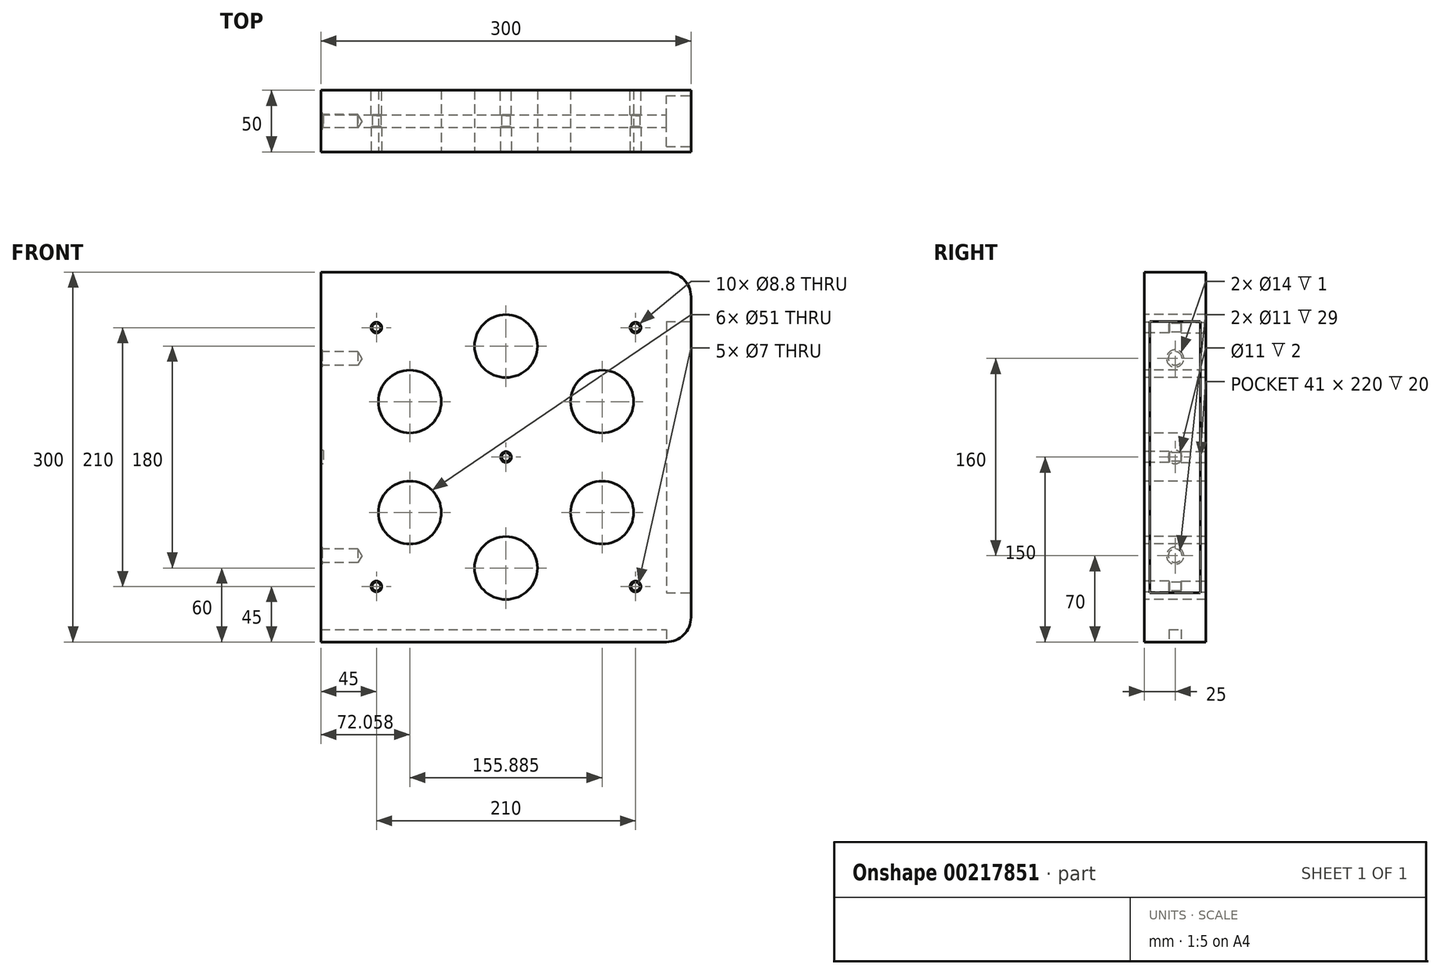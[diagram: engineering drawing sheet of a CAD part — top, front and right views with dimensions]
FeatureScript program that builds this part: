
annotation { "Feature Type Name" : "Feature", "Feature Type Description" : "" }
export const myFeature = defineFeature(function(context is Context, id is Id, definition is map)
    precondition{}
    {
        {
            var Q0;
            Q0=qCreatedBy(makeId("Front.planeOp"),FACE);
            var sketch = newSketch(context, id + "F0", { "sketchPlane" : qUnion([Q0])});
            skLineSegment(sketch, "E0.bottom", {"start": v(-150, 150) * mm, "end": v(150, 150) * mm});
            skLineSegment(sketch, "E0.top", {"start": v(-150, -150) * mm, "end": v(150, -150) * mm});
            skLineSegment(sketch, "E0.left", {"start": v(-150, 150) * mm, "end": v(-150, -150) * mm});
            skLineSegment(sketch, "E0.right", {"start": v(150, 150) * mm, "end": v(150, -150) * mm});
            skPoint(sketch, "E0.middle", {"position": v(0, 0) * mm});
            skSolve(sketch);
        }
        {
            var Q0;
            Q0=qSketchRegion(id+"F0",true);
            extrude(context, id + "F1", {"entities" : qUnion([Q0]), "depth" : 50 * mm});
        }
        {
            var Q0;
            Q0=makeQuery(id+"F1.opExtrude","CAP_FACE",FACE,{"disambiguationData":[OSD([sQuery(id+"F0.wireOp",EDGE,"E0.bottom"),sQuery(id+"F0.wireOp",EDGE,"E0.top"),sQuery(id+"F0.wireOp",EDGE,"E0.left"),sQuery(id+"F0.wireOp",EDGE,"E0.right")])],"isStart":false});
            var sketch = newSketch(context, id + "F2", { "sketchPlane" : qUnion([Q0])});
            skCircle(sketch, "E1", {"center": v(0, 0) * mm, "radius": 90 * mm});
            skLineSegment(sketch, "E2", {"start": v(0, 0) * mm, "end": v(0, 0) * mm});
            skLineSegment(sketch, "E3", {"start": v(0, 0) * mm, "end": v(0, -110.46) * mm});
            skCircle(sketch, "E4", {"center": v(0, 90) * mm, "radius": 25.5 * mm});
            skCircle(sketch, "E5", {"center": v(0, -90) * mm, "radius": 25.5 * mm});
            skLineSegment(sketch, "E6", {"start": v(0, 0) * mm, "end": v(-107.4, 62) * mm});
            skLineSegment(sketch, "E7", {"start": v(0, 0) * mm, "end": v(96.5, -55.7) * mm});
            skLineSegment(sketch, "E8", {"start": v(0, 0) * mm, "end": v(105.95, 61.17) * mm});
            skLineSegment(sketch, "E9", {"start": v(0, 0) * mm, "end": v(-94.57, -54.6) * mm});
            skLineSegment(sketch, "E10", {"start": v(0, 0) * mm, "end": v(0, 104.5) * mm});
            skCircle(sketch, "E11", {"center": v(-77.94, 45) * mm, "radius": 25.5 * mm});
            skCircle(sketch, "E12", {"center": v(-77.94, -45) * mm, "radius": 25.5 * mm});
            skCircle(sketch, "E13", {"center": v(77.94, -45) * mm, "radius": 25.5 * mm});
            skCircle(sketch, "E14", {"center": v(77.94, 45) * mm, "radius": 25.5 * mm});
            skSolve(sketch);
        }
        {
            var Q0;
            {var subQ0=sQuery(id+"F2.wireOp",EDGE,"E8");var subQ1=sQuery(id+"F2.wireOp",EDGE,"E1");var subQ2=makeQuery(id+"F2.imprint","INTERSECT",VERTEX,{"derivedFrom":[subQ1,subQ0]});Q0=makeQuery(id+"F2.imprint","IMPRINT",FACE,{"disambiguationData":[TD([[makeQuery(id+"F2.imprint","IMPRINT",EDGE,{"disambiguationData":[TD([[subQ2,1.0]])],"derivedFrom":subQ1}),1.0]])]});}
            var Q1;
            {var subQ0=sQuery(id+"F2.wireOp",EDGE,"E8");var subQ1=sQuery(id+"F2.wireOp",EDGE,"E1");var subQ2=makeQuery(id+"F2.imprint","INTERSECT",VERTEX,{"derivedFrom":[subQ1,subQ0]});Q1=makeQuery(id+"F2.imprint","IMPRINT",FACE,{"disambiguationData":[TD([[makeQuery(id+"F2.imprint","IMPRINT",EDGE,{"disambiguationData":[TD([[subQ2,1.0]])],"derivedFrom":subQ1}),-1.0]])]});}
            var Q2;
            {var subQ0=sQuery(id+"F2.wireOp",EDGE,"E8");var subQ1=sQuery(id+"F2.wireOp",EDGE,"E1");var subQ2=makeQuery(id+"F2.imprint","INTERSECT",VERTEX,{"derivedFrom":[subQ1,subQ0]});Q2=makeQuery(id+"F2.imprint","IMPRINT",FACE,{"disambiguationData":[TD([[makeQuery(id+"F2.imprint","IMPRINT",EDGE,{"disambiguationData":[TD([[subQ2,-1.0]])],"derivedFrom":subQ1}),1.0]])]});}
            var Q3;
            {var subQ0=sQuery(id+"F2.wireOp",EDGE,"E8");var subQ1=sQuery(id+"F2.wireOp",EDGE,"E1");var subQ2=makeQuery(id+"F2.imprint","INTERSECT",VERTEX,{"derivedFrom":[subQ1,subQ0]});Q3=makeQuery(id+"F2.imprint","IMPRINT",FACE,{"disambiguationData":[TD([[makeQuery(id+"F2.imprint","IMPRINT",EDGE,{"disambiguationData":[TD([[subQ2,-1.0]])],"derivedFrom":subQ1}),-1.0]])]});}
            var Q4;
            {var subQ0=sQuery(id+"F2.wireOp",EDGE,"E1");var subQ1=makeQuery(id+"F2.imprint","INTERSECT",VERTEX,{"derivedFrom":[subQ0,sQuery(id+"F2.wireOp",EDGE,"E10")]});Q4=makeQuery(id+"F2.imprint","IMPRINT",FACE,{"disambiguationData":[TD([[makeQuery(id+"F2.imprint","IMPRINT",EDGE,{"disambiguationData":[TD([[subQ1,1.0]])],"derivedFrom":subQ0}),-1.0]])]});}
            var Q5;
            {var subQ0=sQuery(id+"F2.wireOp",EDGE,"E10");var subQ1=sQuery(id+"F2.wireOp",EDGE,"E1");var subQ2=makeQuery(id+"F2.imprint","INTERSECT",VERTEX,{"derivedFrom":[subQ1,subQ0]});Q5=makeQuery(id+"F2.imprint","IMPRINT",FACE,{"disambiguationData":[TD([[makeQuery(id+"F2.imprint","IMPRINT",EDGE,{"disambiguationData":[TD([[subQ2,1.0]])],"derivedFrom":subQ1}),1.0]])]});}
            var Q6;
            {var subQ0=sQuery(id+"F2.wireOp",EDGE,"E10");var subQ1=sQuery(id+"F2.wireOp",EDGE,"E1");var subQ2=makeQuery(id+"F2.imprint","INTERSECT",VERTEX,{"derivedFrom":[subQ1,subQ0]});Q6=makeQuery(id+"F2.imprint","IMPRINT",FACE,{"disambiguationData":[TD([[makeQuery(id+"F2.imprint","IMPRINT",EDGE,{"disambiguationData":[TD([[subQ2,-1.0]])],"derivedFrom":subQ1}),1.0]])]});}
            var Q7;
            {var subQ0=sQuery(id+"F2.wireOp",EDGE,"E11");var subQ1=sQuery(id+"F2.wireOp",EDGE,"E1");var subQ2=makeQuery(id+"F2.imprint","INTERSECT",VERTEX,{"disambiguationData":[OD(0.0)],"derivedFrom":[subQ1,subQ0]});Q7=makeQuery(id+"F2.imprint","IMPRINT",FACE,{"disambiguationData":[TD([[makeQuery(id+"F2.imprint","IMPRINT",EDGE,{"disambiguationData":[TD([[subQ2,-1.0]])],"derivedFrom":subQ1}),1.0]])]});}
            var Q8;
            {var subQ0=sQuery(id+"F2.wireOp",EDGE,"E11");var subQ1=sQuery(id+"F2.wireOp",EDGE,"E1");var subQ2=makeQuery(id+"F2.imprint","INTERSECT",VERTEX,{"disambiguationData":[OD(0.0)],"derivedFrom":[subQ1,subQ0]});Q8=makeQuery(id+"F2.imprint","IMPRINT",FACE,{"disambiguationData":[TD([[makeQuery(id+"F2.imprint","IMPRINT",EDGE,{"disambiguationData":[TD([[subQ2,-1.0]])],"derivedFrom":subQ1}),-1.0]])]});}
            var Q9;
            {var subQ0=sQuery(id+"F2.wireOp",EDGE,"E6");var subQ1=sQuery(id+"F2.wireOp",EDGE,"E1");var subQ2=makeQuery(id+"F2.imprint","INTERSECT",VERTEX,{"derivedFrom":[subQ1,subQ0]});Q9=makeQuery(id+"F2.imprint","IMPRINT",FACE,{"disambiguationData":[TD([[makeQuery(id+"F2.imprint","IMPRINT",EDGE,{"disambiguationData":[TD([[subQ2,-1.0]])],"derivedFrom":subQ1}),1.0]])]});}
            var Q10;
            {var subQ0=sQuery(id+"F2.wireOp",EDGE,"E6");var subQ1=sQuery(id+"F2.wireOp",EDGE,"E1");var subQ2=makeQuery(id+"F2.imprint","INTERSECT",VERTEX,{"derivedFrom":[subQ1,subQ0]});Q10=makeQuery(id+"F2.imprint","IMPRINT",FACE,{"disambiguationData":[TD([[makeQuery(id+"F2.imprint","IMPRINT",EDGE,{"disambiguationData":[TD([[subQ2,-1.0]])],"derivedFrom":subQ1}),-1.0]])]});}
            var Q11;
            {var subQ0=sQuery(id+"F2.wireOp",EDGE,"E1");var subQ1=makeQuery(id+"F2.imprint","INTERSECT",VERTEX,{"derivedFrom":[subQ0,sQuery(id+"F2.wireOp",EDGE,"E9")]});Q11=makeQuery(id+"F2.imprint","IMPRINT",FACE,{"disambiguationData":[TD([[makeQuery(id+"F2.imprint","IMPRINT",EDGE,{"disambiguationData":[TD([[subQ1,1.0]])],"derivedFrom":subQ0}),-1.0]])]});}
            var Q12;
            {var subQ0=sQuery(id+"F2.wireOp",EDGE,"E9");var subQ1=sQuery(id+"F2.wireOp",EDGE,"E1");var subQ2=makeQuery(id+"F2.imprint","INTERSECT",VERTEX,{"derivedFrom":[subQ1,subQ0]});Q12=makeQuery(id+"F2.imprint","IMPRINT",FACE,{"disambiguationData":[TD([[makeQuery(id+"F2.imprint","IMPRINT",EDGE,{"disambiguationData":[TD([[subQ2,1.0]])],"derivedFrom":subQ1}),1.0]])]});}
            var Q13;
            {var subQ0=sQuery(id+"F2.wireOp",EDGE,"E9");var subQ1=sQuery(id+"F2.wireOp",EDGE,"E1");var subQ2=makeQuery(id+"F2.imprint","INTERSECT",VERTEX,{"derivedFrom":[subQ1,subQ0]});Q13=makeQuery(id+"F2.imprint","IMPRINT",FACE,{"disambiguationData":[TD([[makeQuery(id+"F2.imprint","IMPRINT",EDGE,{"disambiguationData":[TD([[subQ2,-1.0]])],"derivedFrom":subQ1}),1.0]])]});}
            var Q14;
            {var subQ0=sQuery(id+"F2.wireOp",EDGE,"E1");var subQ1=makeQuery(id+"F2.imprint","INTERSECT",VERTEX,{"derivedFrom":[subQ0,sQuery(id+"F2.wireOp",EDGE,"E3")]});Q14=makeQuery(id+"F2.imprint","IMPRINT",FACE,{"disambiguationData":[TD([[makeQuery(id+"F2.imprint","IMPRINT",EDGE,{"disambiguationData":[TD([[subQ1,1.0]])],"derivedFrom":subQ0}),-1.0]])]});}
            var Q15;
            {var subQ0=sQuery(id+"F2.wireOp",EDGE,"E3");var subQ1=sQuery(id+"F2.wireOp",EDGE,"E1");var subQ2=makeQuery(id+"F2.imprint","INTERSECT",VERTEX,{"derivedFrom":[subQ1,subQ0]});Q15=makeQuery(id+"F2.imprint","IMPRINT",FACE,{"disambiguationData":[TD([[makeQuery(id+"F2.imprint","IMPRINT",EDGE,{"disambiguationData":[TD([[subQ2,1.0]])],"derivedFrom":subQ1}),1.0]])]});}
            var Q16;
            {var subQ0=sQuery(id+"F2.wireOp",EDGE,"E3");var subQ1=sQuery(id+"F2.wireOp",EDGE,"E1");var subQ2=makeQuery(id+"F2.imprint","INTERSECT",VERTEX,{"derivedFrom":[subQ1,subQ0]});Q16=makeQuery(id+"F2.imprint","IMPRINT",FACE,{"disambiguationData":[TD([[makeQuery(id+"F2.imprint","IMPRINT",EDGE,{"disambiguationData":[TD([[subQ2,-1.0]])],"derivedFrom":subQ1}),1.0]])]});}
            var Q17;
            {var subQ0=sQuery(id+"F2.wireOp",EDGE,"E1");var subQ1=makeQuery(id+"F2.imprint","INTERSECT",VERTEX,{"derivedFrom":[subQ0,sQuery(id+"F2.wireOp",EDGE,"E7")]});Q17=makeQuery(id+"F2.imprint","IMPRINT",FACE,{"disambiguationData":[TD([[makeQuery(id+"F2.imprint","IMPRINT",EDGE,{"disambiguationData":[TD([[subQ1,1.0]])],"derivedFrom":subQ0}),-1.0]])]});}
            var Q18;
            {var subQ0=sQuery(id+"F2.wireOp",EDGE,"E7");var subQ1=sQuery(id+"F2.wireOp",EDGE,"E1");var subQ2=makeQuery(id+"F2.imprint","INTERSECT",VERTEX,{"derivedFrom":[subQ1,subQ0]});Q18=makeQuery(id+"F2.imprint","IMPRINT",FACE,{"disambiguationData":[TD([[makeQuery(id+"F2.imprint","IMPRINT",EDGE,{"disambiguationData":[TD([[subQ2,1.0]])],"derivedFrom":subQ1}),1.0]])]});}
            var Q19;
            {var subQ0=sQuery(id+"F2.wireOp",EDGE,"E7");var subQ1=sQuery(id+"F2.wireOp",EDGE,"E1");var subQ2=makeQuery(id+"F2.imprint","INTERSECT",VERTEX,{"derivedFrom":[subQ1,subQ0]});Q19=makeQuery(id+"F2.imprint","IMPRINT",FACE,{"disambiguationData":[TD([[makeQuery(id+"F2.imprint","IMPRINT",EDGE,{"disambiguationData":[TD([[subQ2,-1.0]])],"derivedFrom":subQ1}),1.0]])]});}
            extrude(context, id + "F3", {"entities" : qUnion([Q0, Q1, Q2, Q3, Q4, Q5, Q6, Q7, Q8, Q9, Q10, Q11, Q12, Q13, Q14, Q15, Q16, Q17, Q18, Q19]), "operationType" : NewBodyOperationType.REMOVE, "oppositeDirection" : true, "depth" : 50 * mm});
        }
        {
            var Q0;
            Q0=makeQuery(id+"F1.opExtrude","SWEPT_FACE",FACE,{"disambiguationData":[OSD([sQuery(id+"F0.wireOp",EDGE,"E0.left")])]});
            var sketch = newSketch(context, id + "F4", { "sketchPlane" : qUnion([Q0])});
            skCircle(sketch, "E15", {"center": v(25, 0) * mm, "radius": 5.5 * mm});
            skSolve(sketch);
        }
        {
            var Q0;
            Q0=qSketchRegion(id+"F4",true);
            extrude(context, id + "F5", {"entities" : qUnion([Q0]), "operationType" : NewBodyOperationType.REMOVE, "oppositeDirection" : true, "depth" : 2 * mm});
        }
        {
            var Q0;
            Q0=makeQuery(id+"F1.opExtrude","SWEPT_FACE",FACE,{"disambiguationData":[OSD([sQuery(id+"F0.wireOp",EDGE,"E0.left")])]});
            var sketch = newSketch(context, id + "F6", { "sketchPlane" : qUnion([Q0])});
            skCircle(sketch, "E16", {"center": v(25, 80) * mm, "radius": 6 * mm});
            skCircle(sketch, "E17", {"center": v(25, -80) * mm, "radius": 6 * mm});
            skSolve(sketch);
        }
        {
            var Q0;
            Q0=sQuery(id+"F6.wireOp",VERTEX,"E16.center");
            var Q1;
            Q1=sQuery(id+"F6.wireOp",VERTEX,"E17.center");
            var Q2;
            Q2=makeQuery(id+"F1.opExtrude","SWEPT_BODY",BODY,{"disambiguationData":[OSD([sQuery(id+"F0.wireOp",EDGE,"E0.bottom"),sQuery(id+"F0.wireOp",EDGE,"E0.top"),sQuery(id+"F0.wireOp",EDGE,"E0.left"),sQuery(id+"F0.wireOp",EDGE,"E0.right")])]});
            hole(context, id + "F7", {"style" : HoleStyle.SIMPLE, "endStyle" : HoleEndStyle.BLIND, "standardTappedOrClearance" : lookupTablePath({ "standard" : "ISO", "fit" : "Normal", "size" : "M10", "type" : "Clearance" }), "standardBlindInLast" : lookupTablePath({ "fit" : "Standard", "standard" : "ISO", "size" : "M10", "type" : "Clearance" }), "holeDiameter" : 11 * mm, "holeDepth" : 30 * mm, "startFromSketch" : true, "locations" : qUnion([Q0, Q1]), "scope" : qUnion([Q2]), "tappedDepth" : 12 * mm, "tapClearance" : 3});
        }
        {
            var Q0;
            Q0=makeQuery(id+"F1.opExtrude","SWEPT_FACE",FACE,{"disambiguationData":[OSD([sQuery(id+"F0.wireOp",EDGE,"E0.right")])]});
            var sketch = newSketch(context, id + "F8", { "sketchPlane" : qUnion([Q0])});
            skLineSegment(sketch, "E18.bottom", {"start": v(-45.5, 110) * mm, "end": v(-4.5, 110) * mm});
            skLineSegment(sketch, "E18.top", {"start": v(-45.5, -110) * mm, "end": v(-4.5, -110) * mm});
            skLineSegment(sketch, "E18.left", {"start": v(-45.5, 110) * mm, "end": v(-45.5, -110) * mm});
            skLineSegment(sketch, "E18.right", {"start": v(-4.5, 110) * mm, "end": v(-4.5, -110) * mm});
            skSolve(sketch);
        }
        {
            var Q0;
            Q0=qSketchRegion(id+"F8",true);
            extrude(context, id + "F9", {"entities" : qUnion([Q0]), "operationType" : NewBodyOperationType.REMOVE, "oppositeDirection" : true, "depth" : 20 * mm});
        }
        {
            var Q0;
            Q0=makeQuery(id+"F1.opExtrude","CAP_FACE",FACE,{"disambiguationData":[OSD([sQuery(id+"F0.wireOp",EDGE,"E0.bottom"),sQuery(id+"F0.wireOp",EDGE,"E0.top"),sQuery(id+"F0.wireOp",EDGE,"E0.left"),sQuery(id+"F0.wireOp",EDGE,"E0.right")])],"isStart":false});
            var sketch = newSketch(context, id + "F10", { "sketchPlane" : qUnion([Q0])});
            skCircle(sketch, "E19", {"center": v(-105, 105) * mm, "radius": 3.5 * mm});
            skCircle(sketch, "E20", {"center": v(105, 105) * mm, "radius": 3.5 * mm});
            skCircle(sketch, "E21", {"center": v(-105, -105) * mm, "radius": 3.5 * mm});
            skCircle(sketch, "E22", {"center": v(105, -105) * mm, "radius": 3.5 * mm});
            skCircle(sketch, "E23", {"center": v(0, 0) * mm, "radius": 3.5 * mm});
            skSolve(sketch);
        }
        {
            var Q0;
            Q0=qSketchRegion(id+"F10",true);
            extrude(context, id + "F11", {"entities" : qUnion([Q0]), "operationType" : NewBodyOperationType.REMOVE, "oppositeDirection" : true, "depth" : 50 * mm});
        }
        {
            var Q0;
            Q0=makeQuery(id+"F1.opExtrude","SWEPT_EDGE",EDGE,{"disambiguationData":[OSD([sQuery(id+"F0.wireOp",EDGE,"E0.bottom"),sQuery(id+"F0.wireOp",EDGE,"E0.right")])]});
            var Q1;
            Q1=makeQuery(id+"F1.opExtrude","SWEPT_EDGE",EDGE,{"disambiguationData":[OSD([sQuery(id+"F0.wireOp",EDGE,"E0.top"),sQuery(id+"F0.wireOp",EDGE,"E0.right")])]});
            fillet(context, id + "F12", {"entities" : qUnion([Q0, Q1]), "radius" : 20 * mm, "tangentPropagation" : true, "allowEdgeOverflow" : false});
        }
        {
            var Q0;
            Q0=makeQuery(id+"F1.opExtrude","SWEPT_FACE",FACE,{"disambiguationData":[OSD([sQuery(id+"F0.wireOp",EDGE,"E0.top")])]});
            var sketch = newSketch(context, id + "F13", { "sketchPlane" : qUnion([Q0])});
            skLineSegment(sketch, "E24.bottom", {"start": v(-150, 30) * mm, "end": v(130, 30) * mm});
            skLineSegment(sketch, "E24.top", {"start": v(-150, 20) * mm, "end": v(130, 20) * mm});
            skLineSegment(sketch, "E24.left", {"start": v(-150, 30) * mm, "end": v(-150, 20) * mm});
            skLineSegment(sketch, "E24.right", {"start": v(130, 30) * mm, "end": v(130, 20) * mm});
            skSolve(sketch);
        }
        {
            var Q0;
            Q0=qSketchRegion(id+"F13",true);
            extrude(context, id + "F14", {"entities" : qUnion([Q0]), "operationType" : NewBodyOperationType.REMOVE, "oppositeDirection" : true, "depth" : 10 * mm});
        }
        {
            var Q0;
            Q0=makeQuery(id+"F1.opExtrude","CAP_FACE",FACE,{"disambiguationData":[OSD([sQuery(id+"F0.wireOp",EDGE,"E0.bottom"),sQuery(id+"F0.wireOp",EDGE,"E0.top"),sQuery(id+"F0.wireOp",EDGE,"E0.left"),sQuery(id+"F0.wireOp",EDGE,"E0.right")])],"isStart":false});
            var sketch = newSketch(context, id + "F15", { "sketchPlane" : qUnion([Q0])});
            skCircle(sketch, "E25", {"center": v(0, 0) * mm, "radius": 4.5 * mm});
            skCircle(sketch, "E26", {"center": v(-105, 105) * mm, "radius": 4.5 * mm});
            skCircle(sketch, "E27", {"center": v(105, 105) * mm, "radius": 4.5 * mm});
            skCircle(sketch, "E28", {"center": v(-105, -105) * mm, "radius": 4.5 * mm});
            skCircle(sketch, "E29", {"center": v(105, -105) * mm, "radius": 4.5 * mm});
            skSolve(sketch);
        }
        {
            var Q0;
            Q0=sQuery(id+"F15.wireOp",VERTEX,"E26.center");
            var Q1;
            Q1=sQuery(id+"F15.wireOp",VERTEX,"E27.center");
            var Q2;
            Q2=sQuery(id+"F15.wireOp",VERTEX,"E25.center");
            var Q3;
            Q3=sQuery(id+"F15.wireOp",VERTEX,"E28.center");
            var Q4;
            Q4=sQuery(id+"F15.wireOp",VERTEX,"E29.center");
            var Q5;
            Q5=makeQuery(id+"F1.opExtrude","SWEPT_BODY",BODY,{"disambiguationData":[OSD([sQuery(id+"F0.wireOp",EDGE,"E0.bottom"),sQuery(id+"F0.wireOp",EDGE,"E0.top"),sQuery(id+"F0.wireOp",EDGE,"E0.left"),sQuery(id+"F0.wireOp",EDGE,"E0.right")])]});
            hole(context, id + "F16", {"style" : HoleStyle.SIMPLE, "endStyle" : HoleEndStyle.BLIND, "standardTappedOrClearance" : lookupTablePath({ "standard" : "ISO", "fit" : "Normal", "size" : "M8", "type" : "Clearance" }), "standardBlindInLast" : lookupTablePath({ "fit" : "Standard", "standard" : "ISO", "size" : "M8", "type" : "Clearance" }), "holeDiameter" : 8.8 * mm, "holeDepth" : 20 * mm, "startFromSketch" : true, "locations" : qUnion([Q0, Q1, Q2, Q3, Q4]), "scope" : qUnion([Q5])});
        }
        {
            var Q0;
            Q0=makeQuery(id+"F1.opExtrude","CAP_FACE",FACE,{"disambiguationData":[OSD([sQuery(id+"F0.wireOp",EDGE,"E0.bottom"),sQuery(id+"F0.wireOp",EDGE,"E0.top"),sQuery(id+"F0.wireOp",EDGE,"E0.left"),sQuery(id+"F0.wireOp",EDGE,"E0.right")])],"isStart":true});
            var sketch = newSketch(context, id + "F17", { "sketchPlane" : qUnion([Q0])});
            skCircle(sketch, "E30", {"center": v(-105, 105) * mm, "radius": 3.5 * mm});
            skCircle(sketch, "E31", {"center": v(105, 105) * mm, "radius": 3.5 * mm});
            skCircle(sketch, "E32", {"center": v(0, 0) * mm, "radius": 3.5 * mm});
            skCircle(sketch, "E33", {"center": v(-105, -105) * mm, "radius": 3.5 * mm});
            skCircle(sketch, "E34", {"center": v(105, -105) * mm, "radius": 3.5 * mm});
            skSolve(sketch);
        }
        {
            var Q0;
            Q0=sQuery(id+"F17.wireOp",VERTEX,"E30.center");
            var Q1;
            Q1=sQuery(id+"F17.wireOp",VERTEX,"E31.center");
            var Q2;
            Q2=sQuery(id+"F17.wireOp",VERTEX,"E32.center");
            var Q3;
            Q3=sQuery(id+"F17.wireOp",VERTEX,"E33.center");
            var Q4;
            Q4=sQuery(id+"F17.wireOp",VERTEX,"E34.center");
            var Q5;
            Q5=makeQuery(id+"F1.opExtrude","SWEPT_BODY",BODY,{"disambiguationData":[OSD([sQuery(id+"F0.wireOp",EDGE,"E0.bottom"),sQuery(id+"F0.wireOp",EDGE,"E0.top"),sQuery(id+"F0.wireOp",EDGE,"E0.left"),sQuery(id+"F0.wireOp",EDGE,"E0.right")])]});
            hole(context, id + "F18", {"style" : HoleStyle.SIMPLE, "endStyle" : HoleEndStyle.BLIND, "standardTappedOrClearance" : lookupTablePath({ "standard" : "ISO", "fit" : "Normal", "size" : "M8", "type" : "Clearance" }), "standardBlindInLast" : lookupTablePath({ "fit" : "Standard", "standard" : "ISO", "size" : "M8", "type" : "Clearance" }), "holeDiameter" : 8.8 * mm, "holeDepth" : 20 * mm, "startFromSketch" : true, "locations" : qUnion([Q0, Q1, Q2, Q3, Q4]), "scope" : qUnion([Q5])});
        }
        {
            var Q0;
            Q0=makeQuery(id+"F1.opExtrude","SWEPT_FACE",FACE,{"disambiguationData":[OSD([sQuery(id+"F0.wireOp",EDGE,"E0.left")])]});
            var sketch = newSketch(context, id + "F19", { "sketchPlane" : qUnion([Q0])});
            skCircle(sketch, "E35", {"center": v(25, 80) * mm, "radius": 7 * mm});
            skCircle(sketch, "E36", {"center": v(25, -80) * mm, "radius": 7 * mm});
            skSolve(sketch);
        }
        {
            var Q0;
            Q0=qSketchRegion(id+"F19",true);
            extrude(context, id + "F20", {"entities" : qUnion([Q0]), "operationType" : NewBodyOperationType.REMOVE, "oppositeDirection" : true, "depth" : 1 * mm});
        }
    });
